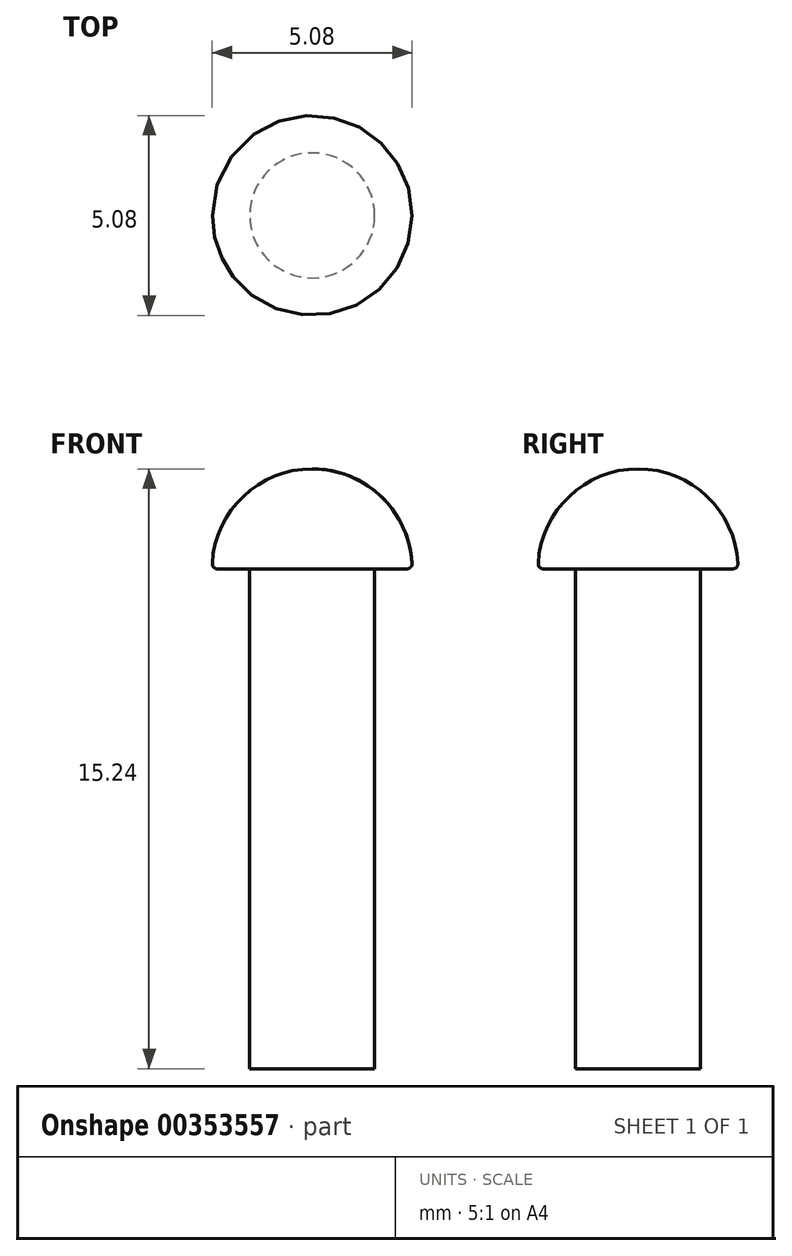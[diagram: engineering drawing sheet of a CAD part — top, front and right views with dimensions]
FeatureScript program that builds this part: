
annotation { "Feature Type Name" : "Feature", "Feature Type Description" : "" }
export const myFeature = defineFeature(function(context is Context, id is Id, definition is map)
    precondition{}
    {
        {
            var Q0;
            Q0=qCreatedBy(makeId("Front.planeOp"),FACE);
            var sketch = newSketch(context, id + "F0", { "sketchPlane" : qUnion([Q0])});
            skArc(sketch, "E0", {"start": v(2.54, 0) * mm, "mid": v(1.8, 1.8) * mm, "end": v(0, 2.54) * mm});
            skLineSegment(sketch, "E1", {"start": v(0, 0) * mm, "end": v(2.54, 0) * mm});
            skLineSegment(sketch, "E2", {"start": v(0, 0) * mm, "end": v(0, 2.54) * mm});
            skPoint(sketch, "E3.orphan", {"position": v(-2.54, 0) * mm});
            skSolve(sketch);
        }
        {
            var Q0;
            Q0 = qSketchRegion(id + "F0", true);
            var Q1;
            Q1=sQuery(id+"F0.wireOp",EDGE,"E2");
            revolve(context, id + "F1", {"entities" : qUnion([Q0]), "axis" : qUnion([Q1]), "revolveType" : RevolveType.FULL});
        }
        {
            var Q0;
            Q0=makeQuery(id+"F1.opRevolve","SWEPT_FACE",FACE,{"disambiguationData":[OSD([sQuery(id+"F0.wireOp",EDGE,"E1")])]});
            var sketch = newSketch(context, id + "F2", { "sketchPlane" : qUnion([Q0])});
            skCircle(sketch, "E4", {"center": v(0, 0) * mm, "radius": 1.59 * mm});
            skSolve(sketch);
        }
        {
            var Q0;
            Q0 = qSketchRegion(id + "F2", true);
            extrude(context, id + "F3", {"entities" : qUnion([Q0]), "operationType" : NewBodyOperationType.ADD, "depth" : 12.7 * mm});
        }
        {
            var Q0;
            Q0=makeQuery(id+"F1.opRevolve","SWEPT_EDGE",EDGE,{"disambiguationData":[OSD([sQuery(id+"F0.wireOp",EDGE,"E0"),sQuery(id+"F0.wireOp",EDGE,"E1")])]});
            fillet(context, id + "F4", {"entities" : qUnion([Q0]), "radius" : 0.13 * mm, "tangentPropagation" : true, "allowEdgeOverflow" : false});
        }
    });
